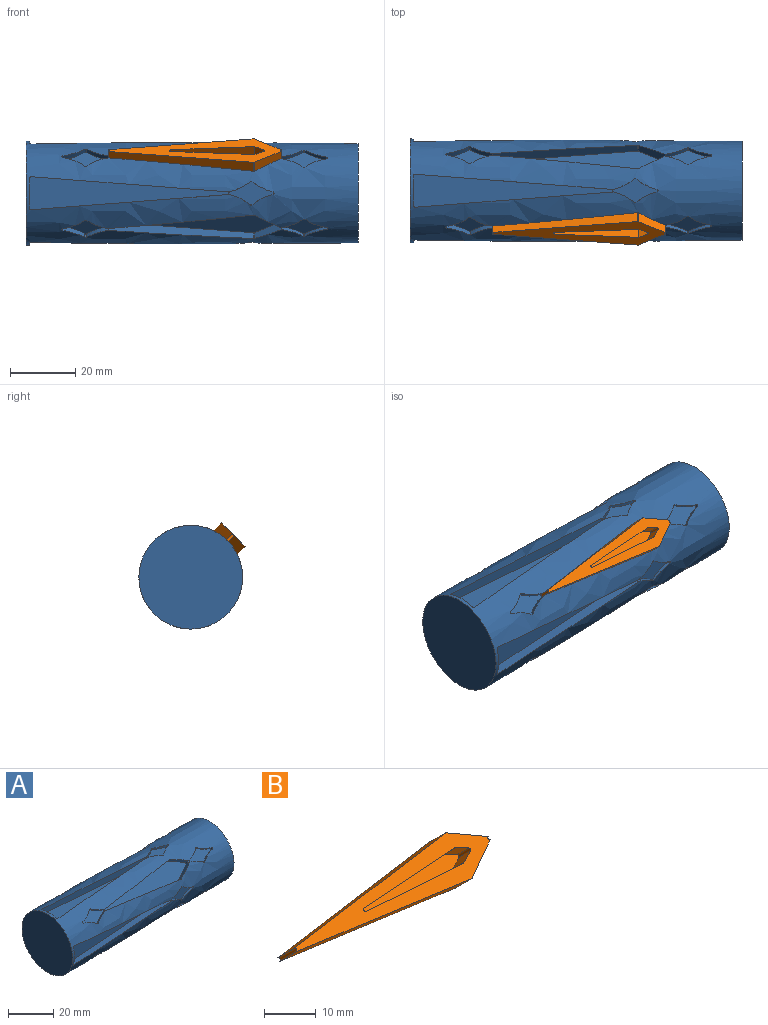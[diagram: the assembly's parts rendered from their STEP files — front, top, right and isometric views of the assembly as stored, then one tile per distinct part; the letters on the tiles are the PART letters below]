
ASSEMBLY  parts=2 mates=1
PART A: 203 faces, bbox 101.6x31.8x31.8 mm
  f0: cylinder r=0.4mm len=1.11mm, axis (0,1,0), area 0.1mm2, adj f8,f9,f42,f150
  f1: cylinder r=0.4mm len=1.11mm, axis (0,1,0), area 0.1mm2, adj f2,f9,f48,f150
  f2: cylinder r=16.51mm len=6.44mm, axis (0,1,0), area 7mm2, adj f1,f3,f9,f150
  f3: cylinder r=0.4mm len=0.64mm, axis (0,1,0), area 0.3mm2, adj f2,f4,f9,f150
  f4: cylinder r=16.51mm len=6.44mm, axis (0,1,0), area 6.6mm2, adj f3,f5,f9,f150
  f5: cylinder r=0.4mm len=1.02mm, axis (0,1,0), area 1.1mm2, adj f4,f6,f9,f150
  f6: cylinder r=16.51mm len=6.44mm, axis (0,1,0), area 6.6mm2, adj f5,f7,f9,f150
  f7: cylinder r=0.4mm len=0.64mm, axis (0,1,0), area 0.3mm2, adj f6,f8,f9,f150
  f8: cylinder r=16.51mm len=6.44mm, axis (0,1,0), area 7mm2, adj f0,f7,f9,f150
  f9: plane 13.99x7.38mm, normal (0,1,0), area 47.8mm2, adj f0,f1,f2,f3,f4,f5,f6,f7
  f10: cylinder r=0.4mm len=0.97mm, axis (0,0.71,0.71), area 0mm2, adj f19,f20,f36,f150
  f11: cylinder r=0.4mm len=1.22mm, axis (0,0.71,0.71), area 0.1mm2, adj f24,f29,f31,f150
  f12: cylinder r=0.4mm len=0.97mm, axis (0,0.71,0.71), area 0mm2, adj f13,f20,f34,f150
  f13: cylinder r=16.51mm len=6.72mm, axis (0,0.71,0.71), area 9.1mm2, adj f12,f14,f20,f150
  f14: cylinder r=0.4mm len=0.69mm, axis (0,0.71,0.71), area 0.5mm2, adj f13,f15,f20,f150
  f15: cylinder r=16.51mm len=6.72mm, axis (0,0.71,0.71), area 8.8mm2, adj f14,f16,f20,f150
  f16: cylinder r=0.4mm len=1.45mm, axis (0,0.71,0.71), area 1.4mm2, adj f15,f17,f20,f150
  f17: cylinder r=16.51mm len=6.72mm, axis (0,0.71,0.71), area 8.8mm2, adj f16,f18,f20,f150
  f18: cylinder r=0.4mm len=0.69mm, axis (0,0.71,0.71), area 0.5mm2, adj f17,f19,f20,f150
  f19: cylinder r=16.51mm len=6.72mm, axis (0,0.71,0.71), area 9.1mm2, adj f10,f18,f20,f150
  f20: plane 14.57x5.22mm, normal (0,0.71,0.71), area 49.3mm2, adj f10,f12,f13,f14,f15,f16,f17,f18
  f21: cylinder r=0.4mm len=1.01mm, axis (0,0.71,0.71), area 0.7mm2, adj f22,f28,f29,f150
  f22: cylinder r=16.51mm len=6.72mm, axis (0,0.71,0.71), area 12.1mm2, adj f21,f23,f29,f150
  f23: cylinder r=0.4mm len=1.22mm, axis (0,0.71,0.71), area 0.1mm2, adj f22,f29,f39,f150
  f24: cylinder r=16.51mm len=6.72mm, axis (0,0.71,0.71), area 12.1mm2, adj f11,f25,f29,f150
  f25: cylinder r=0.4mm len=1.01mm, axis (0,0.71,0.71), area 0.7mm2, adj f24,f26,f29,f150
  f26: cylinder r=16.51mm len=6.72mm, axis (0,0.71,0.71), area 12.5mm2, adj f25,f27,f29,f150
  f27: cylinder r=0.4mm len=1.83mm, axis (0,0.71,0.71), area 2mm2, adj f26,f28,f29,f150
  f28: cylinder r=16.51mm len=6.72mm, axis (0,0.71,0.71), area 12.5mm2, adj f21,f27,f29,f150
  f29: plane 14.57x5.22mm, normal (0,0.71,0.71), area 49.3mm2, adj f11,f21,f22,f23,f24,f25,f26,f27
  f30: cylinder r=0.4mm len=1.89mm, axis (0,0.71,0.71), area 1.9mm2, adj f29,f31,f39,f40
  f31: cylinder r=0.4mm len=2.57mm, axis (0,0.71,0.71), area 0.3mm2, adj f11,f30,f32,f40,f150
  f32: plane 44.34x5.86mm, normal (0.1,-0.7,0.7), area 141.3mm2, adj f31,f33,f40,f150
  f33: cylinder r=0.4mm len=1.8mm, axis (0,0.71,0.71), area 0.6mm2, adj f32,f34,f40,f150
  f34: plane 8.11x5.59mm, normal (-0.5,-0.61,0.61), area 28mm2, adj f12,f33,f35,f40,f150
  f35: cylinder r=0.4mm len=1.89mm, axis (0,0.71,0.71), area 1.9mm2, adj f20,f34,f36,f40
  f36: plane 8.11x5.59mm, normal (-0.5,0.61,-0.61), area 28mm2, adj f10,f35,f37,f40,f150
  f37: cylinder r=0.4mm len=1.8mm, axis (0,0.71,0.71), area 0.6mm2, adj f36,f38,f40,f150
  f38: plane 44.34x5.86mm, normal (0.1,0.7,-0.7), area 141.3mm2, adj f37,f39,f40,f150
  f39: cylinder r=0.4mm len=2.57mm, axis (0,0.71,0.71), area 0.3mm2, adj f23,f30,f38,f40,f150
  f40: plane 52.77x7.17mm, normal (0,0.71,0.71), area 288.3mm2, adj f30,f31,f32,f33,f34,f35,f36,f37
  f41: cylinder r=0.4mm len=2.29mm, axis (0,1,0), area 2mm2, adj f9,f42,f48,f49
  f42: cylinder r=0.4mm len=3.39mm, axis (0,1,0), area 0.5mm2, adj f0,f41,f43,f49,f150
  f43: plane 60.41x4.65mm, normal (-0.08,0,1), area 200.1mm2, adj f42,f44,f49,f150
  f44: cylinder r=0.4mm len=3.11mm, axis (0,1,0), area 2mm2, adj f43,f45,f49,f150
  f45: plane 9.3x3.8mm, normal (1,0,0), area 33.2mm2, adj f44,f46,f49,f150
  f46: cylinder r=0.4mm len=3.11mm, axis (0,1,0), area 2mm2, adj f45,f47,f49,f150
  f47: plane 60.41x4.65mm, normal (-0.08,0,-1), area 200.1mm2, adj f46,f48,f49,f150
  f48: cylinder r=0.4mm len=3.39mm, axis (0,1,0), area 0.5mm2, adj f1,f41,f47,f49,f150
  f49: plane 60.99x10.1mm, normal (0,1,0), area 333.3mm2, adj f41,f42,f43,f44,f45,f46,f47,f48
  f50: cylinder r=0.4mm len=1.11mm, axis (0,0,-1), area 0.1mm2, adj f58,f59,f92,f150
  f51: cylinder r=0.4mm len=1.11mm, axis (0,0,-1), area 0.1mm2, adj f52,f59,f98,f150
  f52: cylinder r=16.51mm len=6.44mm, axis (0,0,-1), area 7mm2, adj f51,f53,f59,f150
  f53: cylinder r=0.4mm len=0.64mm, axis (0,0,-1), area 0.3mm2, adj f52,f54,f59,f150
  f54: cylinder r=16.51mm len=6.44mm, axis (0,0,-1), area 6.6mm2, adj f53,f55,f59,f150
  f55: cylinder r=0.4mm len=1.02mm, axis (0,0,-1), area 1.1mm2, adj f54,f56,f59,f150
  f56: cylinder r=16.51mm len=6.44mm, axis (0,0,-1), area 6.6mm2, adj f55,f57,f59,f150
  f57: cylinder r=0.4mm len=0.64mm, axis (0,0,-1), area 0.3mm2, adj f56,f58,f59,f150
  f58: cylinder r=16.51mm len=6.44mm, axis (0,0,-1), area 7mm2, adj f50,f57,f59,f150
  f59: plane 13.99x7.38mm, normal (0,0,-1), area 47.8mm2, adj f50,f51,f52,f53,f54,f55,f56,f57
  f60: cylinder r=0.4mm len=0.97mm, axis (0,0.71,-0.71), area 0mm2, adj f69,f70,f86,f150
  f61: cylinder r=0.4mm len=1.22mm, axis (0,0.71,-0.71), area 0.1mm2, adj f74,f79,f81,f150
  f62: cylinder r=0.4mm len=0.97mm, axis (0,0.71,-0.71), area 0mm2, adj f63,f70,f84,f150
  f63: cylinder r=16.51mm len=6.72mm, axis (0,0.71,-0.71), area 9.1mm2, adj f62,f64,f70,f150
  f64: cylinder r=0.4mm len=0.69mm, axis (0,0.71,-0.71), area 0.5mm2, adj f63,f65,f70,f150
  f65: cylinder r=16.51mm len=6.72mm, axis (0,0.71,-0.71), area 8.8mm2, adj f64,f66,f70,f150
  f66: cylinder r=0.4mm len=1.45mm, axis (0,0.71,-0.71), area 1.4mm2, adj f65,f67,f70,f150
  f67: cylinder r=16.51mm len=6.72mm, axis (0,0.71,-0.71), area 8.8mm2, adj f66,f68,f70,f150
  f68: cylinder r=0.4mm len=0.69mm, axis (0,0.71,-0.71), area 0.5mm2, adj f67,f69,f70,f150
  f69: cylinder r=16.51mm len=6.72mm, axis (0,0.71,-0.71), area 9.1mm2, adj f60,f68,f70,f150
  f70: plane 14.57x5.22mm, normal (0,0.71,-0.71), area 49.3mm2, adj f60,f62,f63,f64,f65,f66,f67,f68
  f71: cylinder r=0.4mm len=1.01mm, axis (0,0.71,-0.71), area 0.7mm2, adj f72,f78,f79,f150
  f72: cylinder r=16.51mm len=6.72mm, axis (0,0.71,-0.71), area 12.1mm2, adj f71,f73,f79,f150
  f73: cylinder r=0.4mm len=1.22mm, axis (0,0.71,-0.71), area 0.1mm2, adj f72,f79,f89,f150
  f74: cylinder r=16.51mm len=6.72mm, axis (0,0.71,-0.71), area 12.1mm2, adj f61,f75,f79,f150
  f75: cylinder r=0.4mm len=1.01mm, axis (0,0.71,-0.71), area 0.7mm2, adj f74,f76,f79,f150
  f76: cylinder r=16.51mm len=6.72mm, axis (0,0.71,-0.71), area 12.5mm2, adj f75,f77,f79,f150
  f77: cylinder r=0.4mm len=1.83mm, axis (0,0.71,-0.71), area 2mm2, adj f76,f78,f79,f150
  f78: cylinder r=16.51mm len=6.72mm, axis (0,0.71,-0.71), area 12.5mm2, adj f71,f77,f79,f150
  f79: plane 14.57x5.22mm, normal (0,0.71,-0.71), area 49.3mm2, adj f61,f71,f72,f73,f74,f75,f76,f77
  f80: cylinder r=0.4mm len=1.89mm, axis (0,0.71,-0.71), area 1.9mm2, adj f79,f81,f89,f90
  f81: cylinder r=0.4mm len=2.57mm, axis (0,0.71,-0.71), area 0.3mm2, adj f61,f80,f82,f90,f150
  f82: plane 44.34x5.86mm, normal (0.1,0.7,0.7), area 141.3mm2, adj f81,f83,f90,f150
  f83: cylinder r=0.4mm len=1.8mm, axis (0,0.71,-0.71), area 0.6mm2, adj f82,f84,f90,f150
  f84: plane 8.11x5.59mm, normal (-0.5,0.61,0.61), area 28mm2, adj f62,f83,f85,f90,f150
  f85: cylinder r=0.4mm len=1.89mm, axis (0,0.71,-0.71), area 1.9mm2, adj f70,f84,f86,f90
  f86: plane 8.11x5.59mm, normal (-0.5,-0.61,-0.61), area 28mm2, adj f60,f85,f87,f90,f150
  f87: cylinder r=0.4mm len=1.8mm, axis (0,0.71,-0.71), area 0.6mm2, adj f86,f88,f90,f150
  f88: plane 44.34x5.86mm, normal (0.1,-0.7,-0.7), area 141.3mm2, adj f87,f89,f90,f150
  f89: cylinder r=0.4mm len=2.57mm, axis (0,0.71,-0.71), area 0.3mm2, adj f73,f80,f88,f90,f150
  f90: plane 52.77x7.17mm, normal (0,0.71,-0.71), area 288.3mm2, adj f80,f81,f82,f83,f84,f85,f86,f87
  f91: cylinder r=0.4mm len=2.29mm, axis (0,0,-1), area 2mm2, adj f59,f92,f98,f99
  f92: cylinder r=0.4mm len=3.39mm, axis (0,0,-1), area 0.5mm2, adj f50,f91,f93,f99,f150
  f93: plane 60.41x4.65mm, normal (-0.08,1,0), area 200.1mm2, adj f92,f94,f99,f150
  f94: cylinder r=0.4mm len=3.11mm, axis (0,0,-1), area 2mm2, adj f93,f95,f99,f150
  f95: plane 9.3x3.8mm, normal (1,0,0), area 33.2mm2, adj f94,f96,f99,f150
  f96: cylinder r=0.4mm len=3.11mm, axis (0,0,-1), area 2mm2, adj f95,f97,f99,f150
  f97: plane 60.41x4.65mm, normal (-0.08,-1,0), area 200.1mm2, adj f96,f98,f99,f150
  f98: cylinder r=0.4mm len=3.39mm, axis (0,0,-1), area 0.5mm2, adj f51,f91,f97,f99,f150
  f99: plane 60.99x10.1mm, normal (0,0,-1), area 333.3mm2, adj f91,f92,f93,f94,f95,f96,f97,f98
  f100: cylinder r=0.4mm len=1.11mm, axis (0,-1,0), area 0.1mm2, adj f108,f109,f142,f150
  f101: cylinder r=0.4mm len=1.11mm, axis (0,-1,0), area 0.1mm2, adj f102,f109,f148,f150
  f102: cylinder r=16.51mm len=6.44mm, axis (0,-1,0), area 7mm2, adj f101,f103,f109,f150
  f103: cylinder r=0.4mm len=0.64mm, axis (0,-1,0), area 0.3mm2, adj f102,f104,f109,f150
  f104: cylinder r=16.51mm len=6.44mm, axis (0,-1,0), area 6.6mm2, adj f103,f105,f109,f150
  f105: cylinder r=0.4mm len=1.02mm, axis (0,-1,0), area 1.1mm2, adj f104,f106,f109,f150
  f106: cylinder r=16.51mm len=6.44mm, axis (0,-1,0), area 6.6mm2, adj f105,f107,f109,f150
  f107: cylinder r=0.4mm len=0.64mm, axis (0,-1,0), area 0.3mm2, adj f106,f108,f109,f150
  f108: cylinder r=16.51mm len=6.44mm, axis (0,-1,0), area 7mm2, adj f100,f107,f109,f150
  f109: plane 13.99x7.38mm, normal (0,-1,0), area 47.8mm2, adj f100,f101,f102,f103,f104,f105,f106,f107
  f110: cylinder r=0.4mm len=0.97mm, axis (0,-0.71,-0.71), area 0mm2, adj f119,f120,f136,f150
  f111: cylinder r=0.4mm len=1.22mm, axis (0,-0.71,-0.71), area 0.1mm2, adj f124,f129,f131,f150
  f112: cylinder r=0.4mm len=0.97mm, axis (0,-0.71,-0.71), area 0mm2, adj f113,f120,f134,f150
  f113: cylinder r=16.51mm len=6.72mm, axis (0,-0.71,-0.71), area 9.1mm2, adj f112,f114,f120,f150
  f114: cylinder r=0.4mm len=0.69mm, axis (0,-0.71,-0.71), area 0.5mm2, adj f113,f115,f120,f150
  f115: cylinder r=16.51mm len=6.72mm, axis (0,-0.71,-0.71), area 8.8mm2, adj f114,f116,f120,f150
  f116: cylinder r=0.4mm len=1.45mm, axis (0,-0.71,-0.71), area 1.4mm2, adj f115,f117,f120,f150
  f117: cylinder r=16.51mm len=6.72mm, axis (0,-0.71,-0.71), area 8.8mm2, adj f116,f118,f120,f150
  f118: cylinder r=0.4mm len=0.69mm, axis (0,-0.71,-0.71), area 0.5mm2, adj f117,f119,f120,f150
  f119: cylinder r=16.51mm len=6.72mm, axis (0,-0.71,-0.71), area 9.1mm2, adj f110,f118,f120,f150
  f120: plane 14.57x5.22mm, normal (0,-0.71,-0.71), area 49.3mm2, adj f110,f112,f113,f114,f115,f116,f117,f118
  f121: cylinder r=0.4mm len=1.01mm, axis (0,-0.71,-0.71), area 0.7mm2, adj f122,f128,f129,f150
  f122: cylinder r=16.51mm len=6.72mm, axis (0,-0.71,-0.71), area 12.1mm2, adj f121,f123,f129,f150
  f123: cylinder r=0.4mm len=1.22mm, axis (0,-0.71,-0.71), area 0.1mm2, adj f122,f129,f139,f150
  f124: cylinder r=16.51mm len=6.72mm, axis (0,-0.71,-0.71), area 12.1mm2, adj f111,f125,f129,f150
  f125: cylinder r=0.4mm len=1.01mm, axis (0,-0.71,-0.71), area 0.7mm2, adj f124,f126,f129,f150
  f126: cylinder r=16.51mm len=6.72mm, axis (0,-0.71,-0.71), area 12.5mm2, adj f125,f127,f129,f150
  f127: cylinder r=0.4mm len=1.83mm, axis (0,-0.71,-0.71), area 2mm2, adj f126,f128,f129,f150
  f128: cylinder r=16.51mm len=6.72mm, axis (0,-0.71,-0.71), area 12.5mm2, adj f121,f127,f129,f150
  f129: plane 14.57x5.22mm, normal (0,-0.71,-0.71), area 49.3mm2, adj f111,f121,f122,f123,f124,f125,f126,f127
  f130: cylinder r=0.4mm len=1.89mm, axis (0,-0.71,-0.71), area 1.9mm2, adj f129,f131,f139,f140
  f131: cylinder r=0.4mm len=2.57mm, axis (0,-0.71,-0.71), area 0.3mm2, adj f111,f130,f132,f140,f150
  f132: plane 44.34x5.86mm, normal (0.1,0.7,-0.7), area 141.3mm2, adj f131,f133,f140,f150
  f133: cylinder r=0.4mm len=1.8mm, axis (0,-0.71,-0.71), area 0.6mm2, adj f132,f134,f140,f150
  f134: plane 8.11x5.59mm, normal (-0.5,0.61,-0.61), area 28mm2, adj f112,f133,f135,f140,f150
  f135: cylinder r=0.4mm len=1.89mm, axis (0,-0.71,-0.71), area 1.9mm2, adj f120,f134,f136,f140
  f136: plane 8.11x5.59mm, normal (-0.5,-0.61,0.61), area 28mm2, adj f110,f135,f137,f140,f150
  f137: cylinder r=0.4mm len=1.8mm, axis (0,-0.71,-0.71), area 0.6mm2, adj f136,f138,f140,f150
  f138: plane 44.34x5.86mm, normal (0.1,-0.7,0.7), area 141.3mm2, adj f137,f139,f140,f150
  f139: cylinder r=0.4mm len=2.57mm, axis (0,-0.71,-0.71), area 0.3mm2, adj f123,f130,f138,f140,f150
  f140: plane 52.77x7.17mm, normal (0,-0.71,-0.71), area 288.3mm2, adj f130,f131,f132,f133,f134,f135,f136,f137
  f141: cylinder r=0.4mm len=2.29mm, axis (0,-1,0), area 2mm2, adj f109,f142,f148,f149
  f142: cylinder r=0.4mm len=3.39mm, axis (0,-1,0), area 0.5mm2, adj f100,f141,f143,f149,f150
  f143: plane 60.41x4.65mm, normal (-0.08,0,-1), area 200.1mm2, adj f142,f144,f149,f150
  f144: cylinder r=0.4mm len=3.11mm, axis (0,-1,0), area 2mm2, adj f143,f145,f149,f150
  f145: plane 9.3x3.8mm, normal (1,0,0), area 33.2mm2, adj f144,f146,f149,f150
  f146: cylinder r=0.4mm len=3.11mm, axis (0,-1,0), area 2mm2, adj f145,f147,f149,f150
  f147: plane 60.41x4.65mm, normal (-0.08,0,1), area 200.1mm2, adj f146,f148,f149,f150
  f148: cylinder r=0.4mm len=3.39mm, axis (0,-1,0), area 0.5mm2, adj f101,f141,f147,f149,f150
  f149: plane 60.99x10.1mm, normal (0,-1,0), area 333.3mm2, adj f141,f142,f143,f144,f145,f146,f147,f148
  f150: cone r=15.88mm half-angle=0.4deg, axis (-1,0,0), area 6822.1mm2, adj f0,f1,f2,f3,f4,f5,f6,f7
  f151: plane 31.75x31.75mm, normal (-1,0,0), area 791.7mm2, adj f150
  f152: plane 30.4x30.4mm, normal (1,0,0), area 726mm2, adj f150
  f153: cylinder r=0.4mm len=2.29mm, axis (0,0,1), area 2mm2, adj f154,f160,f161,f202
  f154: cylinder r=0.4mm len=3.39mm, axis (0,0,1), area 0.5mm2, adj f150,f153,f155,f161,f193
  f155: plane 60.41x4.65mm, normal (-0.08,-1,0), area 200.1mm2, adj f150,f154,f156,f161
  f156: cylinder r=0.4mm len=3.11mm, axis (0,0,1), area 2mm2, adj f150,f155,f157,f161
  f157: plane 9.3x3.8mm, normal (1,0,0), area 33.2mm2, adj f150,f156,f158,f161
  f158: cylinder r=0.4mm len=3.11mm, axis (0,0,1), area 2mm2, adj f150,f157,f159,f161
  f159: plane 60.41x4.65mm, normal (-0.08,1,0), area 200.1mm2, adj f150,f158,f160,f161
  f160: cylinder r=0.4mm len=3.39mm, axis (0,0,1), area 0.5mm2, adj f150,f153,f159,f161,f195
  f161: plane 60.99x10.1mm, normal (0,0,1), area 333.3mm2, adj f153,f154,f155,f156,f157,f158,f159,f160
  f162: cylinder r=0.4mm len=1.89mm, axis (0,-0.71,0.71), area 1.9mm2, adj f163,f171,f172,f192
  f163: cylinder r=0.4mm len=2.57mm, axis (0,-0.71,0.71), area 0.3mm2, adj f150,f162,f164,f172,f183
  f164: plane 44.34x5.86mm, normal (0.1,-0.7,-0.7), area 141.3mm2, adj f150,f163,f165,f172
  f165: cylinder r=0.4mm len=1.8mm, axis (0,-0.71,0.71), area 0.6mm2, adj f150,f164,f166,f172
  f166: plane 8.11x5.59mm, normal (-0.5,-0.61,-0.61), area 28mm2, adj f150,f165,f167,f172,f175
  f167: cylinder r=0.4mm len=1.89mm, axis (0,-0.71,0.71), area 1.9mm2, adj f166,f168,f172,f182
  f168: plane 8.11x5.59mm, normal (-0.5,0.61,0.61), area 28mm2, adj f150,f167,f169,f172,f173
  f169: cylinder r=0.4mm len=1.8mm, axis (0,-0.71,0.71), area 0.6mm2, adj f150,f168,f170,f172
  f170: plane 44.34x5.86mm, normal (0.1,0.7,0.7), area 141.3mm2, adj f150,f169,f171,f172
  f171: cylinder r=0.4mm len=2.57mm, axis (0,-0.71,0.71), area 0.3mm2, adj f150,f162,f170,f172,f184
  f172: plane 52.77x7.17mm, normal (0,-0.71,0.71), area 288.3mm2, adj f162,f163,f164,f165,f166,f167,f168,f169
  f173: cylinder r=0.4mm len=0.97mm, axis (0,-0.71,0.71), area 0mm2, adj f150,f168,f174,f182
  f174: cylinder r=16.51mm len=6.72mm, axis (0,-0.71,0.71), area 9.1mm2, adj f150,f173,f181,f182
  f175: cylinder r=0.4mm len=0.97mm, axis (0,-0.71,0.71), area 0mm2, adj f150,f166,f176,f182
  f176: cylinder r=16.51mm len=6.72mm, axis (0,-0.71,0.71), area 9.1mm2, adj f150,f175,f177,f182
  f177: cylinder r=0.4mm len=0.69mm, axis (0,-0.71,0.71), area 0.5mm2, adj f150,f176,f178,f182
  f178: cylinder r=16.51mm len=6.72mm, axis (0,-0.71,0.71), area 8.8mm2, adj f150,f177,f179,f182
  f179: cylinder r=0.4mm len=1.45mm, axis (0,-0.71,0.71), area 1.4mm2, adj f150,f178,f180,f182
  f180: cylinder r=16.51mm len=6.72mm, axis (0,-0.71,0.71), area 8.8mm2, adj f150,f179,f181,f182
  f181: cylinder r=0.4mm len=0.69mm, axis (0,-0.71,0.71), area 0.5mm2, adj f150,f174,f180,f182
  f182: plane 14.57x5.22mm, normal (0,-0.71,0.71), area 49.3mm2, adj f167,f173,f174,f175,f176,f177,f178,f179
  f183: cylinder r=0.4mm len=1.22mm, axis (0,-0.71,0.71), area 0.1mm2, adj f150,f163,f191,f192
  f184: cylinder r=0.4mm len=1.22mm, axis (0,-0.71,0.71), area 0.1mm2, adj f150,f171,f185,f192
  f185: cylinder r=16.51mm len=6.72mm, axis (0,-0.71,0.71), area 12.1mm2, adj f150,f184,f186,f192
  f186: cylinder r=0.4mm len=1.01mm, axis (0,-0.71,0.71), area 0.7mm2, adj f150,f185,f187,f192
  f187: cylinder r=16.51mm len=6.72mm, axis (0,-0.71,0.71), area 12.5mm2, adj f150,f186,f188,f192
  f188: cylinder r=0.4mm len=1.83mm, axis (0,-0.71,0.71), area 2mm2, adj f150,f187,f189,f192
  f189: cylinder r=16.51mm len=6.72mm, axis (0,-0.71,0.71), area 12.5mm2, adj f150,f188,f190,f192
  f190: cylinder r=0.4mm len=1.01mm, axis (0,-0.71,0.71), area 0.7mm2, adj f150,f189,f191,f192
  f191: cylinder r=16.51mm len=6.72mm, axis (0,-0.71,0.71), area 12.1mm2, adj f150,f183,f190,f192
  f192: plane 14.57x5.22mm, normal (0,-0.71,0.71), area 49.3mm2, adj f162,f183,f184,f185,f186,f187,f188,f189
  f193: cylinder r=0.4mm len=1.11mm, axis (0,0,1), area 0.1mm2, adj f150,f154,f194,f202
  f194: cylinder r=16.51mm len=6.44mm, axis (0,0,1), area 7mm2, adj f150,f193,f201,f202
  f195: cylinder r=0.4mm len=1.11mm, axis (0,0,1), area 0.1mm2, adj f150,f160,f196,f202
  f196: cylinder r=16.51mm len=6.44mm, axis (0,0,1), area 7mm2, adj f150,f195,f197,f202
  f197: cylinder r=0.4mm len=0.64mm, axis (0,0,1), area 0.3mm2, adj f150,f196,f198,f202
  f198: cylinder r=16.51mm len=6.44mm, axis (0,0,1), area 6.6mm2, adj f150,f197,f199,f202
  f199: cylinder r=0.4mm len=1.02mm, axis (0,0,1), area 1.1mm2, adj f150,f198,f200,f202
  f200: cylinder r=16.51mm len=6.44mm, axis (0,0,1), area 6.6mm2, adj f150,f199,f201,f202
  f201: cylinder r=0.4mm len=0.64mm, axis (0,0,1), area 0.3mm2, adj f150,f194,f200,f202
  f202: plane 13.99x7.38mm, normal (0,0,1), area 47.8mm2, adj f153,f193,f194,f195,f196,f197,f198,f199
PART B: 21 faces, bbox 52.8x11.7x11.7 mm
  f0: plane 52.77x7.17mm, normal (0,-0.71,0.71), area 227.9mm2, adj f1,f2,f3,f4,f5,f6,f7,f8
  f1: cylinder r=0.4mm len=5.03mm, axis (0,0.71,-0.71), area 6.4mm2, adj f0,f2,f10,f11
  f2: cylinder r=0.4mm len=4.5mm, axis (0,0.71,-0.71), area 0.5mm2, adj f0,f1,f3,f11
  f3: plane 44.34x7.79mm, normal (-0.1,0.7,0.7), area 283.1mm2, adj f0,f2,f4,f11
  f4: cylinder r=0.4mm len=4.53mm, axis (0,0.71,-0.71), area 1.6mm2, adj f0,f3,f5,f11
  f5: plane 8.11x7.77mm, normal (0.5,0.61,0.61), area 59.3mm2, adj f0,f4,f6,f11
  f6: cylinder r=0.4mm len=5.03mm, axis (0,0.71,-0.71), area 6.4mm2, adj f0,f5,f7,f11
  f7: plane 8.11x7.77mm, normal (0.5,-0.61,-0.61), area 59.3mm2, adj f0,f6,f8,f11
  f8: cylinder r=0.4mm len=4.53mm, axis (0,0.71,-0.71), area 1.6mm2, adj f0,f7,f9,f11
  f9: plane 44.34x7.79mm, normal (-0.1,-0.7,-0.7), area 283.1mm2, adj f0,f8,f10,f11
  f10: cylinder r=0.4mm len=4.5mm, axis (0,0.71,-0.71), area 0.5mm2, adj f0,f1,f9,f11
  f11: plane 52.77x7.17mm, normal (0,0.71,-0.71), area 288.3mm2, adj f1,f2,f3,f4,f5,f6,f7,f8
  f12: plane 25.52x4.08mm, normal (0.05,-0.71,-0.71), area 113.6mm2, adj f0,f13,f19,f20
  f13: cylinder r=0.4mm len=3.71mm, axis (0,-0.71,0.71), area 5.4mm2, adj f0,f12,f14,f20
  f14: plane 25.52x4.08mm, normal (0.05,0.71,0.71), area 113.6mm2, adj f0,f13,f15,f20
  f15: cylinder r=0.4mm len=3.17mm, axis (0,-0.71,0.71), area 0.9mm2, adj f0,f14,f16,f20
  f16: plane 4.08x4.08mm, normal (-0.45,0.63,0.63), area 13.2mm2, adj f0,f15,f17,f20
  f17: cylinder r=0.4mm len=3.65mm, axis (0,-0.71,0.71), area 3.9mm2, adj f0,f16,f18,f20
  f18: plane 4.08x4.08mm, normal (-0.45,-0.63,-0.63), area 13.2mm2, adj f0,f17,f19,f20
  f19: cylinder r=0.4mm len=3.17mm, axis (0,-0.71,0.71), area 0.9mm2, adj f0,f12,f18,f20
  f20: plane 28.97x2.43mm, normal (0,-0.71,0.71), area 60.4mm2, adj f12,f13,f14,f15,f16,f17,f18,f19
PLACE A t=(-63.12,18,0.32)mm
PLACE B t=(-63.12,20.7,-2.37)mm
MATE fastened A.f172 <-> B.f11  axis (0,-0.71,0.71) through (-6.24,9.46,8.87)mm
